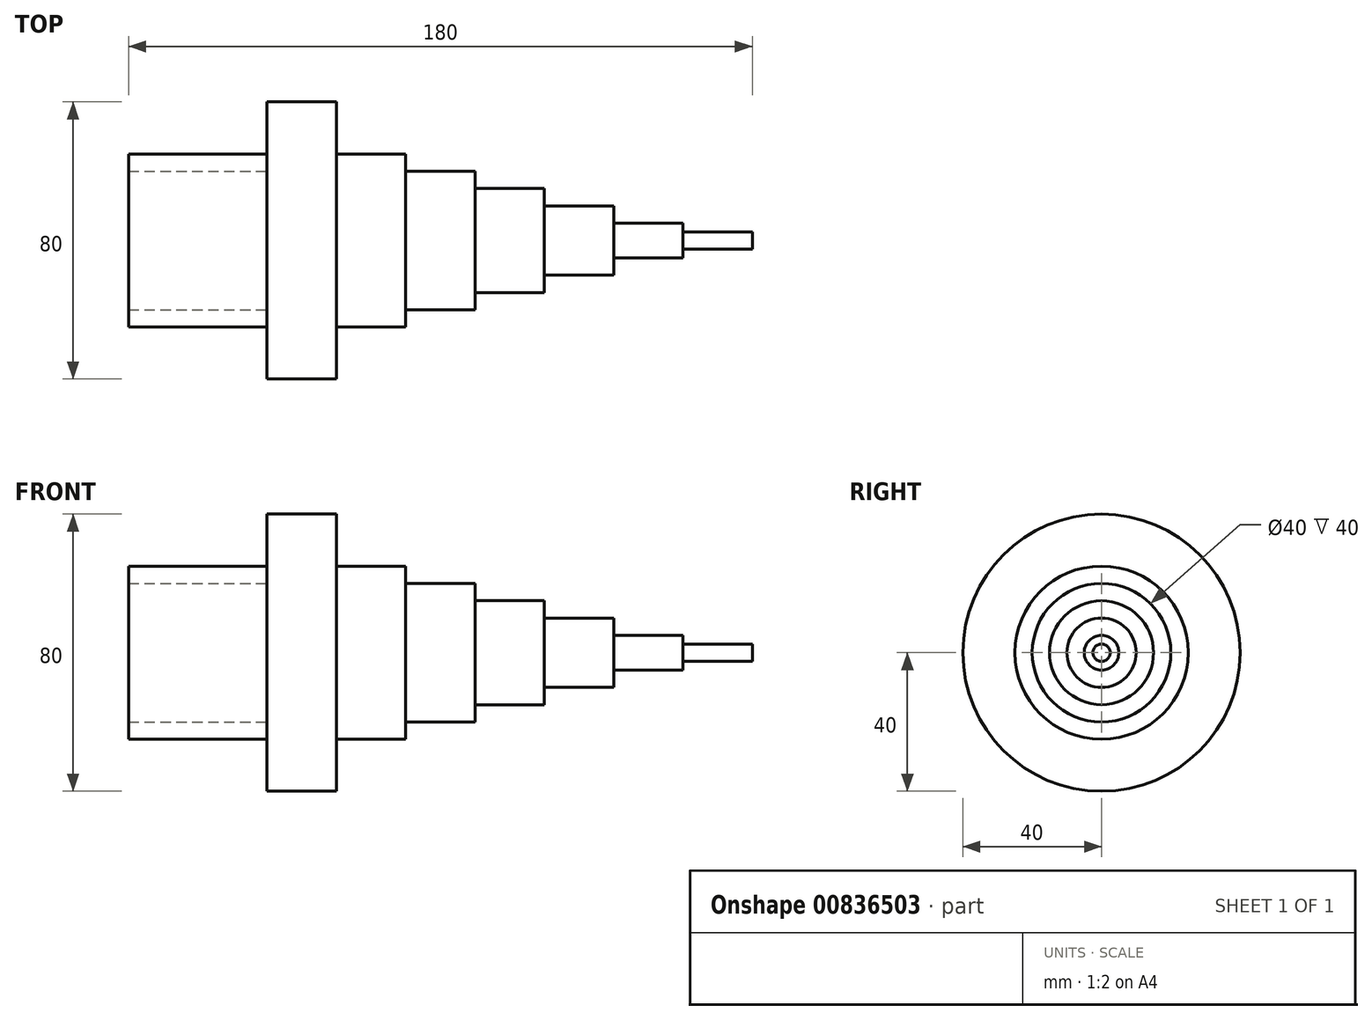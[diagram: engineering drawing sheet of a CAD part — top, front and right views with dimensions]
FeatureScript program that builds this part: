
annotation { "Feature Type Name" : "Feature", "Feature Type Description" : "" }
export const myFeature = defineFeature(function(context is Context, id is Id, definition is map)
    precondition{}
    {
        {
            var Q0;
            Q0=qCreatedBy(makeId("Top.planeOp"),FACE);
            var sketch = newSketch(context, id + "F0", { "sketchPlane" : qUnion([Q0])});
            skLineSegment(sketch, "E0.bottom", {"start": v(10, 0) * mm, "end": v(-10, 0) * mm});
            skLineSegment(sketch, "E0.top", {"start": v(10, 20) * mm, "end": v(-10, 20) * mm});
            skLineSegment(sketch, "E0.left", {"start": v(10, 0) * mm, "end": v(10, 20) * mm});
            skLineSegment(sketch, "E0.right", {"start": v(-10, 0) * mm, "end": v(-10, 20) * mm});
            skPoint(sketch, "E0.middle", {"position": v(0, 10) * mm});
            skLineSegment(sketch, "E1.bottom", {"start": v(10, 0) * mm, "end": v(30, 0) * mm});
            skLineSegment(sketch, "E1.top", {"start": v(10, 15) * mm, "end": v(30, 15) * mm});
            skLineSegment(sketch, "E1.left", {"start": v(10, 0) * mm, "end": v(10, 15) * mm});
            skLineSegment(sketch, "E1.right", {"start": v(30, 0) * mm, "end": v(30, 15) * mm});
            skLineSegment(sketch, "E2.bottom", {"start": v(30, 0) * mm, "end": v(50, 0) * mm});
            skLineSegment(sketch, "E2.top", {"start": v(30, 10) * mm, "end": v(50, 10) * mm});
            skLineSegment(sketch, "E2.left", {"start": v(30, 0) * mm, "end": v(30, 10) * mm});
            skLineSegment(sketch, "E2.right", {"start": v(50, 0) * mm, "end": v(50, 10) * mm});
            skPoint(sketch, "E3.oppositeSnap0", {"position": v(50, 5) * mm});
            skLineSegment(sketch, "E3.bottom", {"start": v(50, 0) * mm, "end": v(70, 0) * mm});
            skLineSegment(sketch, "E3.top", {"start": v(50, 5) * mm, "end": v(70, 5) * mm});
            skLineSegment(sketch, "E3.left", {"start": v(50, 0) * mm, "end": v(50, 5) * mm});
            skLineSegment(sketch, "E3.right", {"start": v(70, 0) * mm, "end": v(70, 5) * mm});
            skLineSegment(sketch, "E4.bottom", {"start": v(70, 0) * mm, "end": v(90, 0) * mm});
            skLineSegment(sketch, "E4.top", {"start": v(70, 2.5) * mm, "end": v(90, 2.5) * mm});
            skLineSegment(sketch, "E4.left", {"start": v(70, 0) * mm, "end": v(70, 2.5) * mm});
            skLineSegment(sketch, "E4.right", {"start": v(90, 0) * mm, "end": v(90, 2.5) * mm});
            skLineSegment(sketch, "E5.bottom", {"start": v(-10, 0) * mm, "end": v(-30, 0) * mm});
            skLineSegment(sketch, "E5.top", {"start": v(-10, 25) * mm, "end": v(-30, 25) * mm});
            skLineSegment(sketch, "E5.left", {"start": v(-10, 0) * mm, "end": v(-10, 25) * mm});
            skLineSegment(sketch, "E5.right", {"start": v(-30, 0) * mm, "end": v(-30, 25) * mm});
            skLineSegment(sketch, "E6.bottom", {"start": v(-30, 0) * mm, "end": v(-50, 0) * mm});
            skLineSegment(sketch, "E6.top", {"start": v(-30, 40) * mm, "end": v(-50, 40) * mm});
            skLineSegment(sketch, "E6.left", {"start": v(-30, 0) * mm, "end": v(-30, 40) * mm});
            skLineSegment(sketch, "E6.right", {"start": v(-50, 0) * mm, "end": v(-50, 40) * mm});
            skLineSegment(sketch, "E7.bottom", {"start": v(-50, 25) * mm, "end": v(-90, 25) * mm});
            skLineSegment(sketch, "E7.top", {"start": v(-50, 20) * mm, "end": v(-90, 20) * mm});
            skLineSegment(sketch, "E7.left", {"start": v(-50, 25) * mm, "end": v(-50, 20) * mm});
            skLineSegment(sketch, "E7.right", {"start": v(-90, 25) * mm, "end": v(-90, 20) * mm});
            skSolve(sketch);
        }
        {
            var Q0;
            {var subQ3=sQuery(id+"F0.wireOp",EDGE,"E6.bottom");Q0=makeQuery(id+"F0.imprint","IMPRINT",FACE,{"disambiguationData":[TD([[makeQuery(id+"F0.imprint","IMPRINT",EDGE,{"derivedFrom":subQ3}),-1.0]])]});}
            var Q1;
            Q1=makeQuery(id+"F0.imprint","IMPRINT",FACE,{"disambiguationData":[TD([[makeQuery(id+"F0.imprint","IMPRINT",EDGE,{"derivedFrom":sQuery(id+"F0.wireOp",EDGE,"E7.bottom")}),1.0]])]});
            var Q2;
            {var subQ3=sQuery(id+"F0.wireOp",EDGE,"E5.bottom");Q2=makeQuery(id+"F0.imprint","IMPRINT",FACE,{"disambiguationData":[TD([[makeQuery(id+"F0.imprint","IMPRINT",EDGE,{"derivedFrom":subQ3}),-1.0]])]});}
            var Q3;
            {var subQ1=sQuery(id+"F0.wireOp",EDGE,"E0.bottom");Q3=makeQuery(id+"F0.imprint","IMPRINT",FACE,{"disambiguationData":[TD([[makeQuery(id+"F0.imprint","IMPRINT",EDGE,{"derivedFrom":subQ1}),-1.0]])]});}
            var Q4;
            Q4=makeQuery(id+"F0.imprint","IMPRINT",FACE,{"disambiguationData":[TD([[makeQuery(id+"F0.imprint","IMPRINT",EDGE,{"derivedFrom":sQuery(id+"F0.wireOp",EDGE,"E1.bottom")}),1.0]])]});
            var Q5;
            Q5=makeQuery(id+"F0.imprint","IMPRINT",FACE,{"disambiguationData":[TD([[makeQuery(id+"F0.imprint","IMPRINT",EDGE,{"derivedFrom":sQuery(id+"F0.wireOp",EDGE,"E2.bottom")}),1.0]])]});
            var Q6;
            Q6=makeQuery(id+"F0.imprint","IMPRINT",FACE,{"disambiguationData":[TD([[makeQuery(id+"F0.imprint","IMPRINT",EDGE,{"derivedFrom":sQuery(id+"F0.wireOp",EDGE,"E3.bottom")}),1.0]])]});
            var Q7;
            Q7=makeQuery(id+"F0.imprint","IMPRINT",FACE,{"disambiguationData":[TD([[makeQuery(id+"F0.imprint","IMPRINT",EDGE,{"derivedFrom":sQuery(id+"F0.wireOp",EDGE,"E4.bottom")}),1.0]])]});
            var Q8;
            Q8=sQuery(id+"F0.wireOp",EDGE,"E6.bottom");
            revolve(context, id + "F1", {"surfaceOperationType" : NewSurfaceOperationType.NEW, "entities" : qUnion([Q0, Q1, Q2, Q3, Q4, Q5, Q6, Q7]), "axis" : qUnion([Q8]), "revolveType" : RevolveType.FULL});
        }
    });
